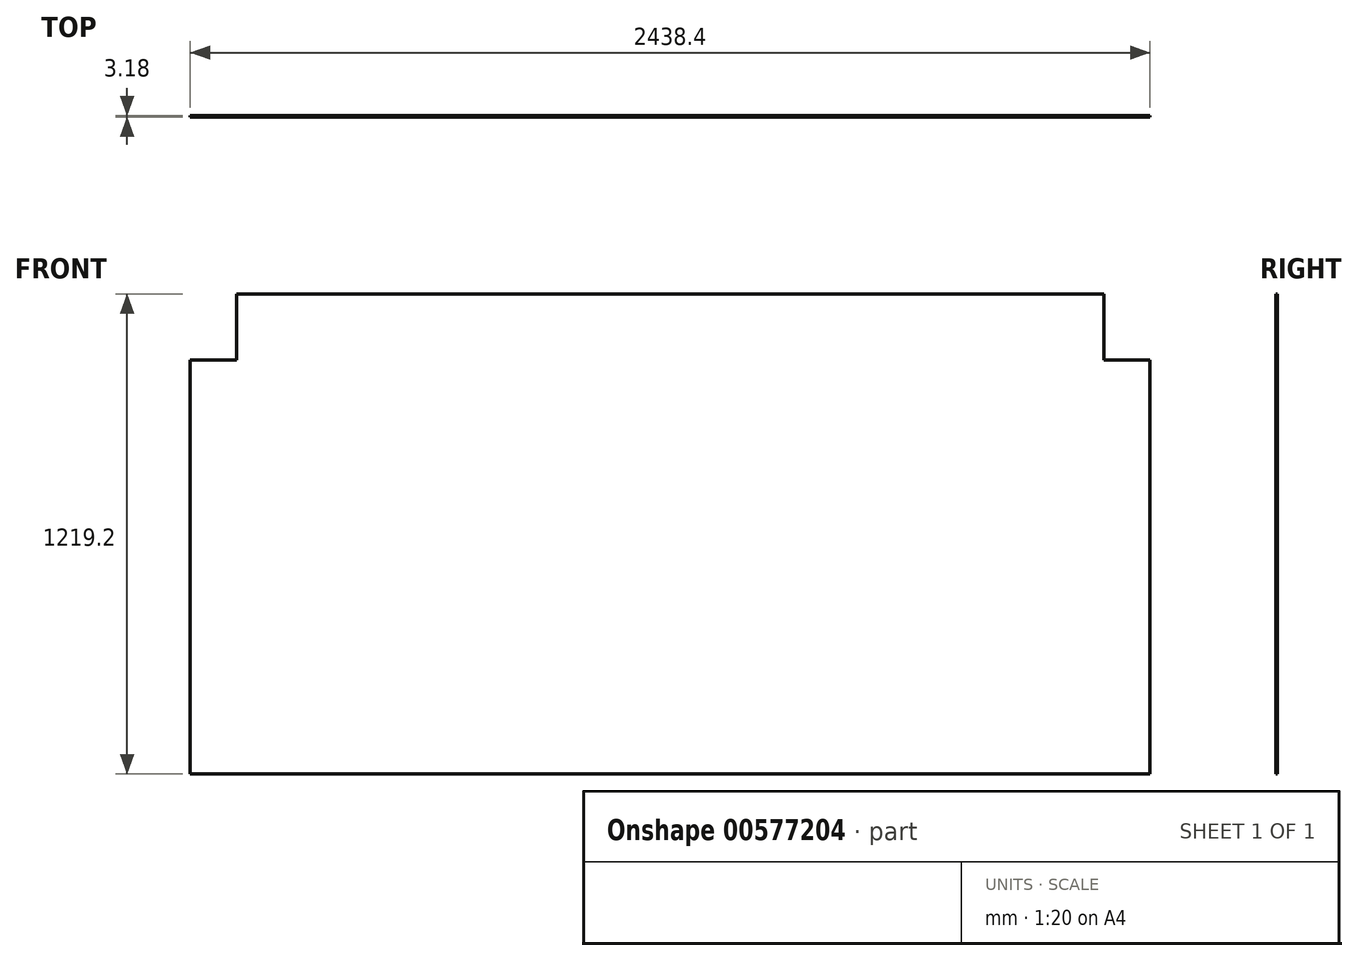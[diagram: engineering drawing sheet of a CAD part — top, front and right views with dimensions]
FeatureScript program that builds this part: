
annotation { "Feature Type Name" : "Feature", "Feature Type Description" : "" }
export const myFeature = defineFeature(function(context is Context, id is Id, definition is map)
    precondition{}
    {
        {
            var Q0;
            Q0=qCreatedBy(makeId("Front.planeOp"),FACE);
            var sketch = newSketch(context, id + "F0", { "sketchPlane" : qUnion([Q0])});
            skLineSegment(sketch, "E0.bottom", {"start": v(0, 0) * mm, "end": v(2438.4, 0) * mm});
            skLineSegment(sketch, "E0.top", {"start": v(0, 1219.2) * mm, "end": v(2438.4, 1219.2) * mm});
            skLineSegment(sketch, "E0.left", {"start": v(0, 0) * mm, "end": v(0, 1219.2) * mm});
            skLineSegment(sketch, "E0.right", {"start": v(2438.4, 0) * mm, "end": v(2438.4, 1219.2) * mm});
            skSolve(sketch);
        }
        {
            var Q0;
            Q0 = qSketchRegion(id + "F0", true);
            extrude(context, id + "F1", {"entities" : qUnion([Q0]), "depth" : 3.17 * mm, "offsetDistance" : 25.4 * mm});
        }
        {
            var Q0;
            Q0=makeQuery(id+"F1.opExtrude","CAP_FACE",FACE,{"disambiguationData":[OSD([sQuery(id+"F0.wireOp",EDGE,"E0.bottom"),sQuery(id+"F0.wireOp",EDGE,"E0.top"),sQuery(id+"F0.wireOp",EDGE,"E0.left"),sQuery(id+"F0.wireOp",EDGE,"E0.right")])],"isStart":false});
            var sketch = newSketch(context, id + "F2", { "sketchPlane" : qUnion([Q0])});
            skLineSegment(sketch, "E1.bottom", {"start": v(0, 1219.2) * mm, "end": v(117.48, 1219.2) * mm});
            skLineSegment(sketch, "E1.top", {"start": v(0, 1050.92) * mm, "end": v(117.48, 1050.92) * mm});
            skLineSegment(sketch, "E1.left", {"start": v(0, 1219.2) * mm, "end": v(0, 1050.92) * mm});
            skLineSegment(sketch, "E1.right", {"start": v(117.48, 1219.2) * mm, "end": v(117.48, 1050.92) * mm});
            skLineSegment(sketch, "E2.bottom", {"start": v(2438.4, 1219.2) * mm, "end": v(2320.92, 1219.2) * mm});
            skLineSegment(sketch, "E2.top", {"start": v(2438.4, 1050.93) * mm, "end": v(2320.92, 1050.93) * mm});
            skLineSegment(sketch, "E2.left", {"start": v(2438.4, 1219.2) * mm, "end": v(2438.4, 1050.93) * mm});
            skLineSegment(sketch, "E2.right", {"start": v(2320.92, 1219.2) * mm, "end": v(2320.92, 1050.93) * mm});
            skSolve(sketch);
        }
        {
            var Q0;
            Q0 = qSketchRegion(id + "F2", true);
            extrude(context, id + "F3", {"entities" : qUnion([Q0]), "operationType" : NewBodyOperationType.REMOVE, "oppositeDirection" : true, "depth" : 25.4 * mm, "offsetDistance" : 25.4 * mm});
        }
    });
